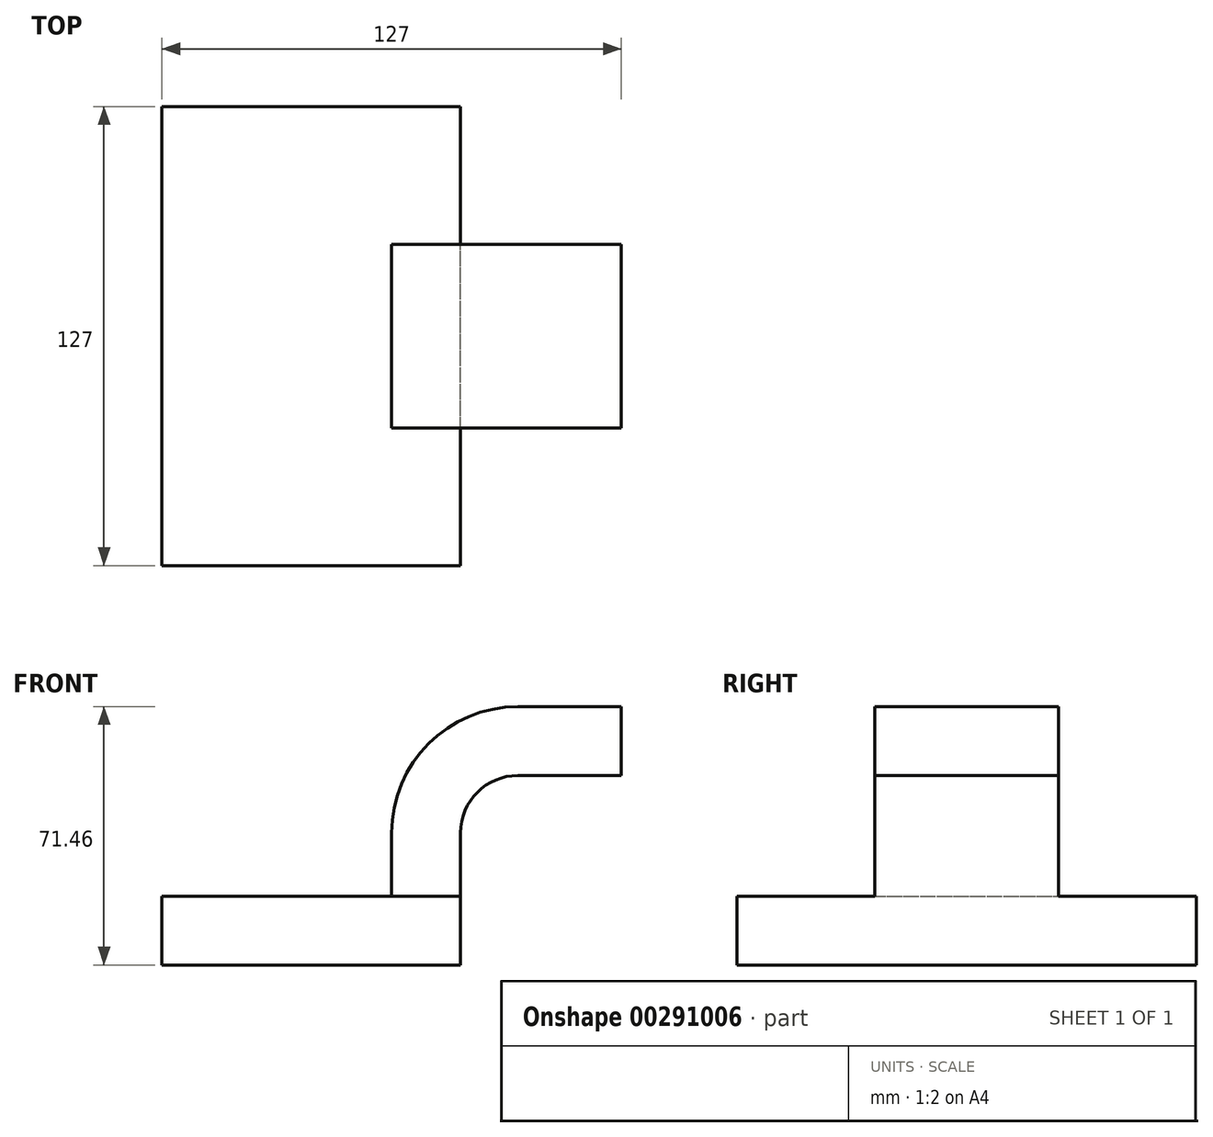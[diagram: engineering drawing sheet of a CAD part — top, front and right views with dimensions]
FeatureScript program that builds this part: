
annotation { "Feature Type Name" : "Feature", "Feature Type Description" : "" }
export const myFeature = defineFeature(function(context is Context, id is Id, definition is map)
    precondition{}
    {
        {
            var Q0;
            Q0=qCreatedBy(makeId("Front.planeOp"),FACE);
            var sketch = newSketch(context, id + "F0", { "sketchPlane" : qUnion([Q0])});
            skLineSegment(sketch, "E0.bottom", {"start": v(-41.28, 9.52) * mm, "end": v(41.28, 9.52) * mm});
            skLineSegment(sketch, "E0.top", {"start": v(-41.28, -9.52) * mm, "end": v(41.27, -9.52) * mm});
            skLineSegment(sketch, "E0.left", {"start": v(-41.28, 9.52) * mm, "end": v(-41.28, -9.52) * mm});
            skLineSegment(sketch, "E0.right", {"start": v(41.28, 9.52) * mm, "end": v(41.27, -9.52) * mm});
            skPoint(sketch, "E0.middle", {"position": v(0, 0) * mm});
            skLineSegment(sketch, "E1.bottom", {"start": v(111.13, 66.68) * mm, "end": v(60.33, 66.68) * mm});
            skLineSegment(sketch, "E1.top", {"start": v(111.13, 38.1) * mm, "end": v(60.33, 38.1) * mm});
            skLineSegment(sketch, "E1.left", {"start": v(111.13, 66.68) * mm, "end": v(111.13, 38.1) * mm});
            skLineSegment(sketch, "E1.right", {"start": v(60.33, 66.68) * mm, "end": v(60.33, 38.1) * mm});
            skPoint(sketch, "E1.middle", {"position": v(85.73, 52.39) * mm});
            skLineSegment(sketch, "E2", {"start": v(41.28, 9.52) * mm, "end": v(41.28, 27) * mm});
            skArc(sketch, "E3", {"start": v(41.27, 27) * mm, "mid": v(45.92, 38.23) * mm, "end": v(57.15, 42.88) * mm});
            skLineSegment(sketch, "E4", {"start": v(57.15, 42.88) * mm, "end": v(85.72, 42.88) * mm});
            skLineSegment(sketch, "E5.0", {"start": v(57.15, 61.93) * mm, "end": v(85.72, 61.93) * mm});
            skArc(sketch, "E5.1", {"start": v(22.22, 27) * mm, "mid": v(32.45, 51.7) * mm, "end": v(57.15, 61.93) * mm});
            skLineSegment(sketch, "E5.2", {"start": v(22.22, 9.52) * mm, "end": v(22.22, 27) * mm});
            skLineSegment(sketch, "E6", {"start": v(85.73, 38.1) * mm, "end": v(85.73, 66.68) * mm});
            skFitSpline(sketch, "E7", {"points": [v(-41.28, 9.52) * mm, v(57.15, 61.93) * mm], "startDerivative": vector(1.53, 150.68) * mm, "endDerivative": vector(143.84, -2.6) * mm});
            skSolve(sketch);
        }
        {
            var Q0;
            Q0=makeQuery(id+"F0.imprint","IMPRINT",FACE,{"disambiguationData":[TD([[makeQuery(id+"F0.imprint","IMPRINT",EDGE,{"derivedFrom":sQuery(id+"F0.wireOp",EDGE,"E0.top")}),1.0]])]});
            extrude(context, id + "F1", {"entities" : qUnion([Q0]), "endBound" : BoundingType.SYMMETRIC, "depth" : 127 * mm});
        }
        {
            var Q0;
            {var subQ1=sQuery(id+"F0.wireOp",EDGE,"E2");Q0=makeQuery(id+"F0.imprint","IMPRINT",FACE,{"disambiguationData":[TD([[makeQuery(id+"F0.imprint","IMPRINT",EDGE,{"derivedFrom":subQ1}),1.0]])]});}
            var Q1;
            {var subQ0=sQuery(id+"F0.wireOp",EDGE,"E5.0");var subQ1=sQuery(id+"F0.wireOp",EDGE,"E1.right");var subQ2=makeQuery(id+"F0.imprint","INTERSECT",VERTEX,{"derivedFrom":[subQ1,subQ0]});Q1=makeQuery(id+"F0.imprint","IMPRINT",FACE,{"disambiguationData":[TD([[makeQuery(id+"F0.imprint","IMPRINT",EDGE,{"disambiguationData":[TD([[subQ2,-1.0]])],"derivedFrom":subQ1}),1.0]])]});}
            extrude(context, id + "F2", {"entities" : qUnion([Q0, Q1]), "operationType" : NewBodyOperationType.ADD, "endBound" : BoundingType.SYMMETRIC, "depth" : 50.8 * mm});
        }
        {
            var Q0;
            Q0=makeQuery(id+"F0.imprint","IMPRINT",FACE,{"disambiguationData":[TD([[makeQuery(id+"F0.imprint","IMPRINT",EDGE,{"derivedFrom":sQuery(id+"F0.wireOp",EDGE,"E5.1")}),1.0]])]});
            extrude(context, id + "F3", {"entities" : qUnion([Q0]), "operationType" : NewBodyOperationType.ADD, "endBound" : BoundingType.SYMMETRIC, "depth" : 15.88 * mm});
        }
    });
